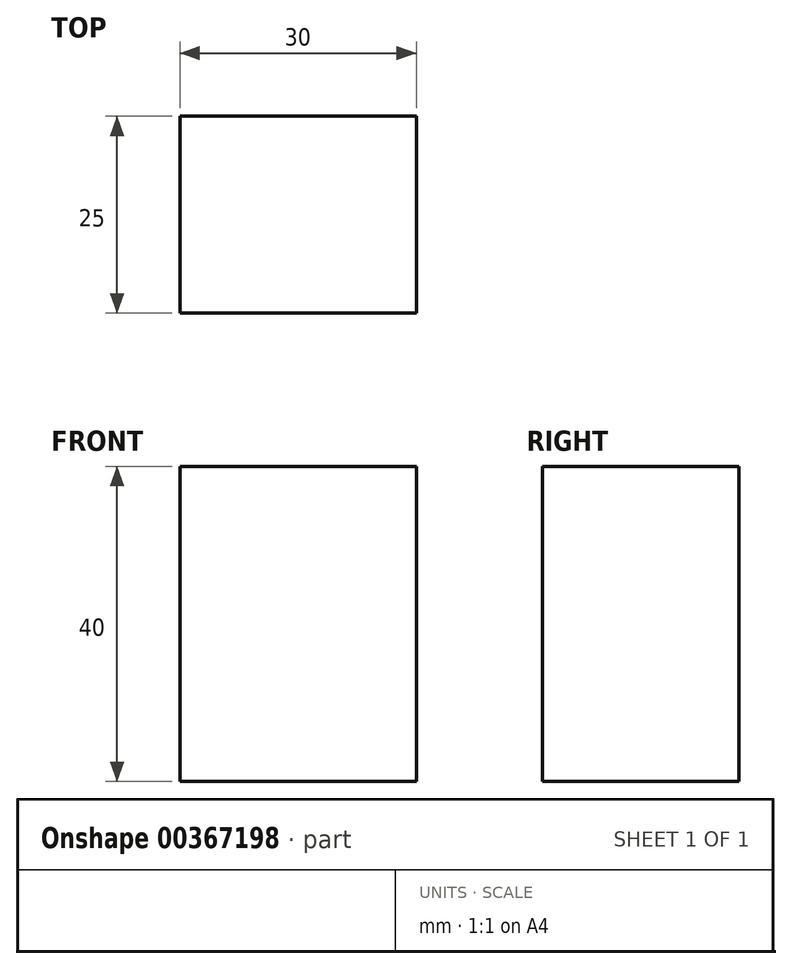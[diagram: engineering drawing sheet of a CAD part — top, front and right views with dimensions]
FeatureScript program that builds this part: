
annotation { "Feature Type Name" : "Feature", "Feature Type Description" : "" }
export const myFeature = defineFeature(function(context is Context, id is Id, definition is map)
    precondition{}
    {
        {
            var Q0;
            Q0=qCreatedBy(makeId("Front.planeOp"),FACE);
            var sketch = newSketch(context, id + "F0", { "sketchPlane" : qUnion([Q0])});
            skLineSegment(sketch, "E0.bottom", {"start": v(0, 0) * mm, "end": v(30, 0) * mm});
            skLineSegment(sketch, "E0.top", {"start": v(0, -40) * mm, "end": v(30, -40) * mm});
            skLineSegment(sketch, "E0.left", {"start": v(0, 0) * mm, "end": v(0, -40) * mm});
            skLineSegment(sketch, "E0.right", {"start": v(30, 0) * mm, "end": v(30, -40) * mm});
            skSolve(sketch);
        }
        {
            var Q0;
            Q0=makeQuery(id+"F0.imprint","IMPRINT",FACE,{"disambiguationData":[TD([[makeQuery(id+"F0.imprint","IMPRINT",EDGE,{"derivedFrom":sQuery(id+"F0.wireOp",EDGE,"E0.bottom")}),-1.0]])]});
            extrude(context, id + "F1", {"entities" : qUnion([Q0]), "depth" : 25 * mm});
        }
    });
